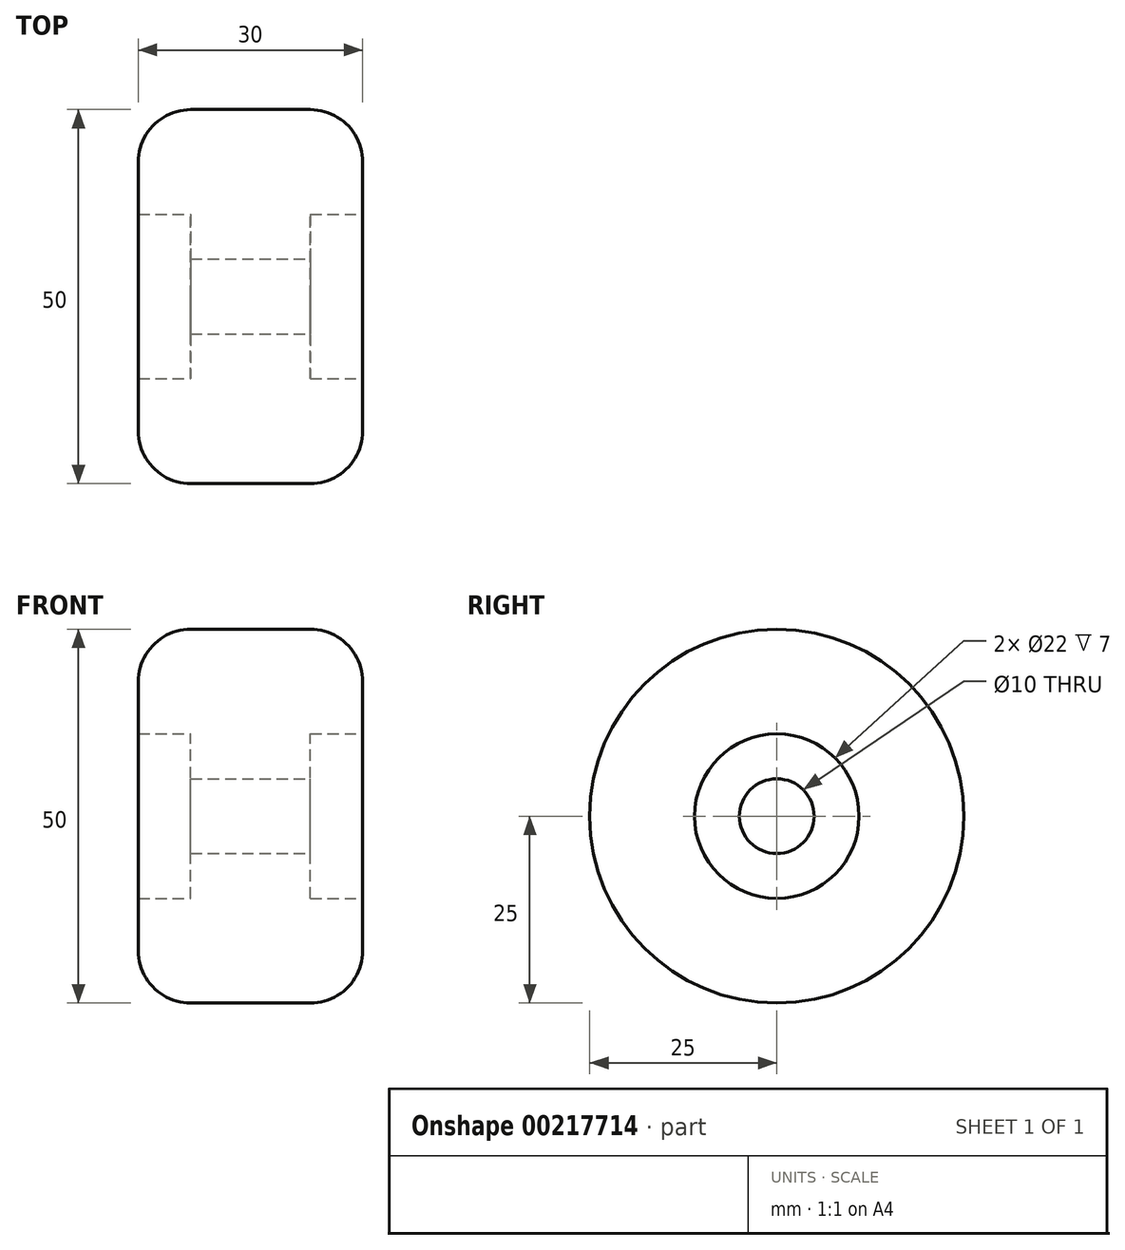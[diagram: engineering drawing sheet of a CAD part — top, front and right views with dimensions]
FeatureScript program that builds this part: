
annotation { "Feature Type Name" : "Feature", "Feature Type Description" : "" }
export const myFeature = defineFeature(function(context is Context, id is Id, definition is map)
    precondition{}
    {
        {
            var Q0;
            Q0=qCreatedBy(makeId("Front.planeOp"),FACE);
            var sketch = newSketch(context, id + "F0", { "sketchPlane" : qUnion([Q0])});
            skLineSegment(sketch, "E0", {"start": v(-8, 0) * mm, "end": v(-8, 5) * mm, "construction": true});
            skLineSegment(sketch, "E1", {"start": v(-8, 11) * mm, "end": v(-15, 11) * mm});
            skLineSegment(sketch, "E2", {"start": v(-15, 11) * mm, "end": v(-15, 18) * mm});
            skArc(sketch, "E3", {"start": v(-15, 18) * mm, "mid": v(-12.95, 22.95) * mm, "end": v(-8, 25) * mm});
            skLineSegment(sketch, "E4", {"start": v(0, 29.58) * mm, "end": v(0, -21.44) * mm, "construction": true});
            skLineSegment(sketch, "E5", {"start": v(-8, 25) * mm, "end": v(0, 25) * mm});
            skLineSegment(sketch, "E6", {"start": v(-8, 5) * mm, "end": v(0, 5) * mm});
            skLineSegment(sketch, "E7", {"start": v(-8, 5) * mm, "end": v(-8, 11) * mm});
            skLineSegment(sketch, "E8.MirrorCS", {"start": v(8, 25) * mm, "end": v(0, 25) * mm});
            skArc(sketch, "E9.MirrorCS", {"start": v(15, 18) * mm, "mid": v(12.95, 22.95) * mm, "end": v(8, 25) * mm});
            skLineSegment(sketch, "E10.MirrorCS", {"start": v(15, 11) * mm, "end": v(15, 18) * mm});
            skLineSegment(sketch, "E11.MirrorCS", {"start": v(8, 11) * mm, "end": v(15, 11) * mm});
            skLineSegment(sketch, "E12.MirrorCS", {"start": v(8, 5) * mm, "end": v(8, 11) * mm});
            skLineSegment(sketch, "E13.MirrorCS", {"start": v(8, 5) * mm, "end": v(0, 5) * mm});
            skLineSegment(sketch, "E14", {"start": v(23.84, 0) * mm, "end": v(-39.16, 0) * mm, "construction": true});
            skSolve(sketch);
        }
        {
            var Q0;
            Q0=makeQuery(id+"F0.imprint","IMPRINT",FACE,{"disambiguationData":[TD([[makeQuery(id+"F0.imprint","IMPRINT",EDGE,{"derivedFrom":sQuery(id+"F0.wireOp",EDGE,"E1")}),-1.0]])]});
            var Q1;
            Q1=sQuery(id+"F0.wireOp",EDGE,"E14");
            revolve(context, id + "F1", {"entities" : qUnion([Q0]), "axis" : qUnion([Q1]), "revolveType" : RevolveType.FULL});
        }
    });
